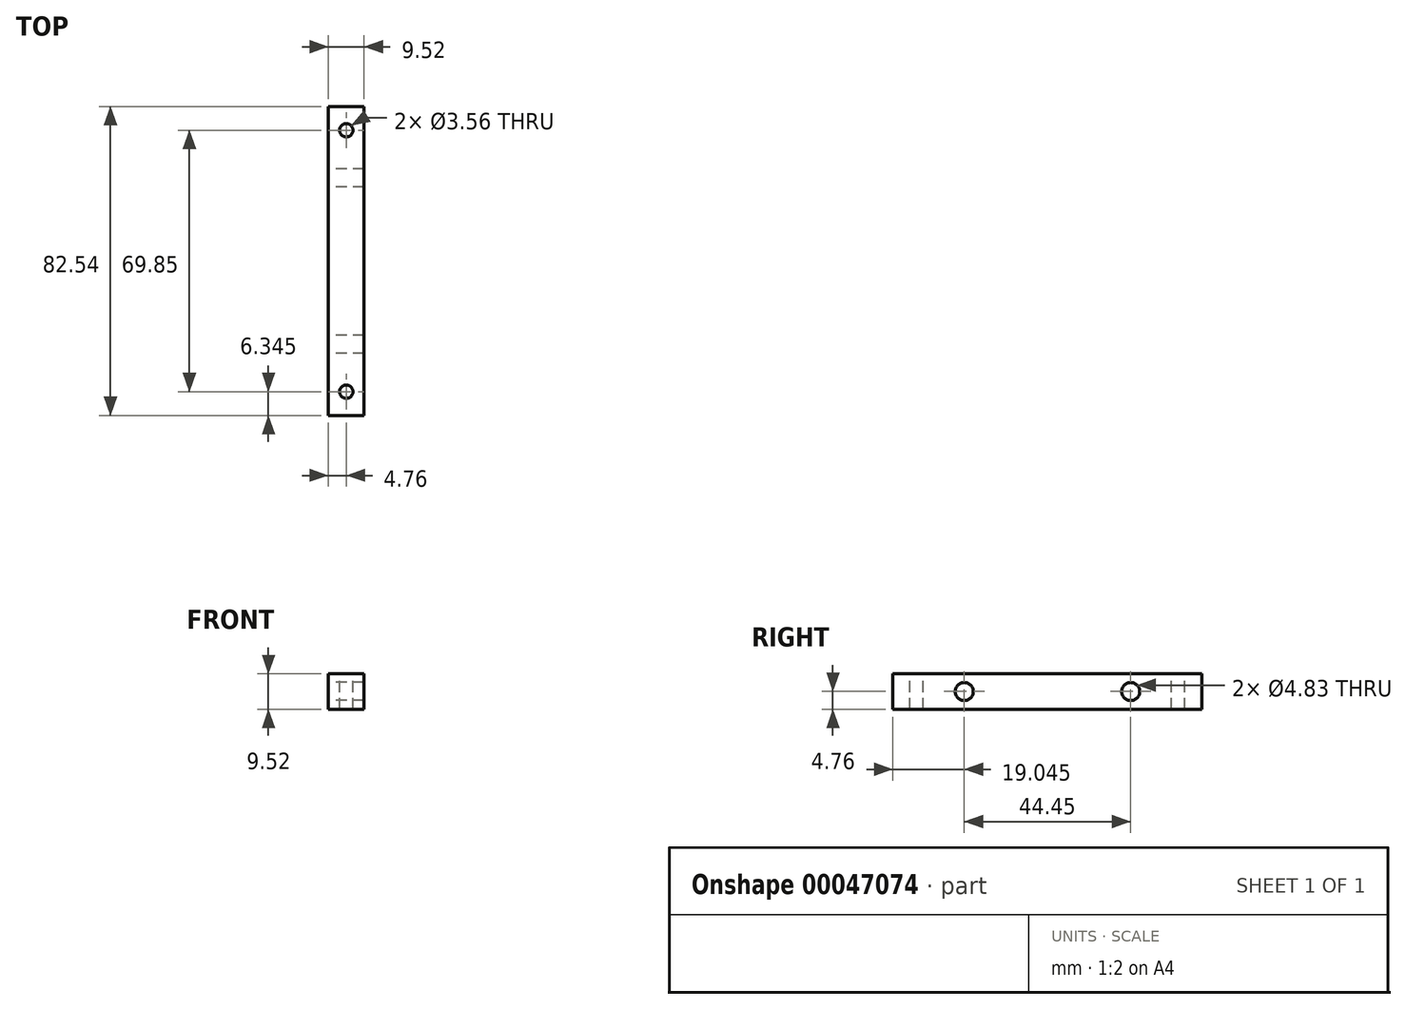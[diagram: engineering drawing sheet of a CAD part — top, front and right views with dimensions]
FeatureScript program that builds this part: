
annotation { "Feature Type Name" : "Feature", "Feature Type Description" : "" }
export const myFeature = defineFeature(function(context is Context, id is Id, definition is map)
    precondition{}
    {
        {
            var Q0;
            Q0=qCreatedBy(makeId("Front.planeOp"),FACE);
            var sketch = newSketch(context, id + "F0", { "sketchPlane" : qUnion([Q0])});
            skLineSegment(sketch, "E0.rect.bottom", {"start": v(4.76, 4.76) * mm, "end": v(-4.76, 4.76) * mm});
            skLineSegment(sketch, "E0.rect.top", {"start": v(4.76, -4.76) * mm, "end": v(-4.76, -4.76) * mm});
            skLineSegment(sketch, "E0.rect.left", {"start": v(4.76, 4.76) * mm, "end": v(4.76, -4.76) * mm});
            skLineSegment(sketch, "E0.rect.right", {"start": v(-4.76, 4.76) * mm, "end": v(-4.76, -4.76) * mm});
            skPoint(sketch, "E0.rect.middle", {"position": v(0, 0) * mm});
            skSolve(sketch);
        }
        {
            var Q0;
            Q0 = qSketchRegion(id + "F0", true);
            extrude(context, id + "F1", {"entities" : qUnion([Q0]), "endBound" : BoundingType.SYMMETRIC, "depth" : 82.55 * mm});
        }
        {
            var Q0;
            Q0=makeQuery(id+"F1.opExtrude","SWEPT_FACE",FACE,{"disambiguationData":[OSD([sQuery(id+"F0.wireOp",EDGE,"E0.rect.bottom")])]});
            var sketch = newSketch(context, id + "F2", { "sketchPlane" : qUnion([Q0])});
            skCircle(sketch, "E1", {"center": v(0, 34.93) * mm, "radius": 1.78 * mm});
            skLineSegment(sketch, "E2", {"start": v(14.89, 0) * mm, "end": v(-15.47, 0) * mm, "construction": true});
            skPoint(sketch, "E2.startSnap0", {"position": v(4.76, 0) * mm});
            skPoint(sketch, "E2.endSnap0", {"position": v(4.76, 0) * mm});
            skCircle(sketch, "E3", {"center": v(0, -34.93) * mm, "radius": 1.78 * mm});
            skSolve(sketch);
        }
        {
            var Q0;
            Q0 = qSketchRegion(id + "F2", true);
            extrude(context, id + "F3", {"entities" : qUnion([Q0]), "operationType" : NewBodyOperationType.REMOVE, "endBound" : BoundingType.THROUGH_ALL, "oppositeDirection" : true, "depth" : 25.4 * mm});
        }
        {
            var Q0;
            Q0=makeQuery(id+"F1.opExtrude","SWEPT_FACE",FACE,{"disambiguationData":[OSD([sQuery(id+"F0.wireOp",EDGE,"E0.rect.right")])]});
            var sketch = newSketch(context, id + "F4", { "sketchPlane" : qUnion([Q0])});
            skCircle(sketch, "E4", {"center": v(-22.23, 0) * mm, "radius": 2.41 * mm});
            skLineSegment(sketch, "E5", {"start": v(0, 11.73) * mm, "end": v(0, -15.6) * mm, "construction": true});
            skPoint(sketch, "E5.endSnap0", {"position": v(0, -4.76) * mm});
            skCircle(sketch, "E6.MirrorC", {"center": v(22.23, 0) * mm, "radius": 2.41 * mm});
            skSolve(sketch);
        }
        {
            var Q0;
            Q0 = qSketchRegion(id + "F4", true);
            extrude(context, id + "F5", {"entities" : qUnion([Q0]), "operationType" : NewBodyOperationType.REMOVE, "endBound" : BoundingType.THROUGH_ALL, "oppositeDirection" : true, "depth" : 25.4 * mm});
        }
    });
